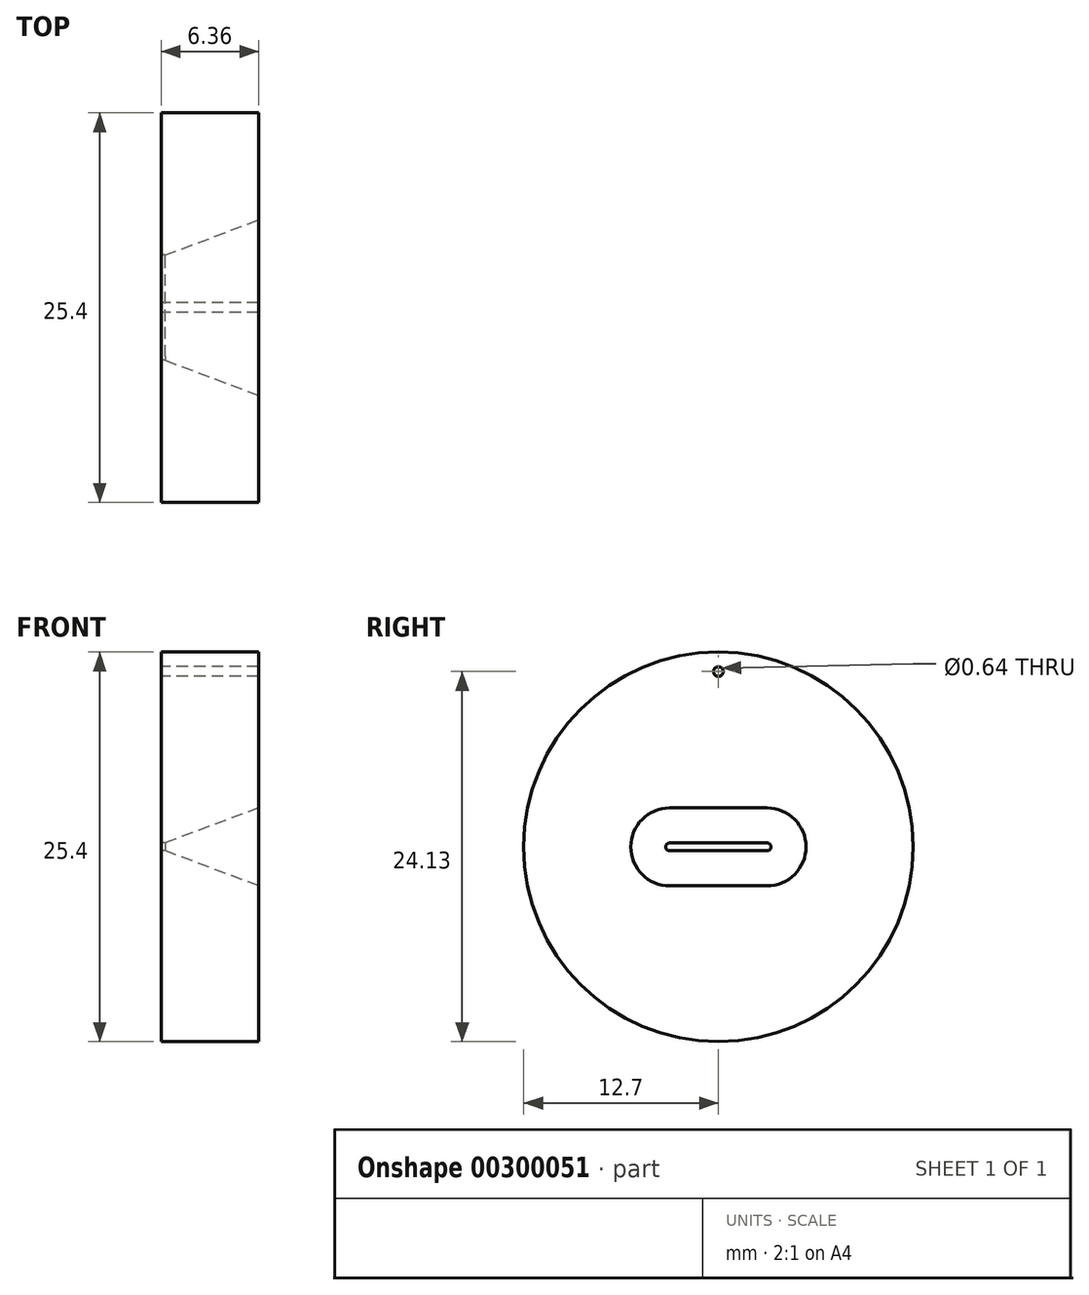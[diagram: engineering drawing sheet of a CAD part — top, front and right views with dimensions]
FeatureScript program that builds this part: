
annotation { "Feature Type Name" : "Feature", "Feature Type Description" : "" }
export const myFeature = defineFeature(function(context is Context, id is Id, definition is map)
    precondition{}
    {
        {
            var Q0;
            Q0=qCreatedBy(makeId("Right.planeOp"),FACE);
            var sketch = newSketch(context, id + "F0", { "sketchPlane" : qUnion([Q0])});
            skCircle(sketch, "E0", {"center": v(0, 0) * mm, "radius": 12.7 * mm});
            skSolve(sketch);
        }
        {
            var Q0;
            Q0 = qSketchRegion(id + "F0", true);
            extrude(context, id + "F1", {"entities" : qUnion([Q0]), "endBound" : BoundingType.SYMMETRIC, "depth" : 6.35 * mm});
        }
        {
            var Q0;
            Q0=makeQuery(id+"F1.opExtrude","CAP_FACE",FACE,{"disambiguationData":[OSD([sQuery(id+"F0.wireOp",EDGE,"E0")])],"isStart":true});
            var sketch = newSketch(context, id + "F2", { "sketchPlane" : qUnion([Q0])});
            skLineSegment(sketch, "E1", {"start": v(0, 13.8) * mm, "end": v(0, -8.5) * mm, "construction": true});
            skCircle(sketch, "E2", {"center": v(0, 11.43) * mm, "radius": 0.32 * mm});
            skSolve(sketch);
        }
        {
            var Q0;
            Q0=qCreatedBy(makeId("Front.planeOp"),FACE);
            var sketch = newSketch(context, id + "F3", { "sketchPlane" : qUnion([Q0])});
            skLineSegment(sketch, "E3", {"start": v(-29.97, 0) * mm, "end": v(27.38, 0) * mm, "construction": true});
            skSolve(sketch);
        }
        {
            var Q0;
            Q0 = qSketchRegion(id + "F2", true);
            extrude(context, id + "F4", {"entities" : qUnion([Q0]), "operationType" : NewBodyOperationType.REMOVE, "endBound" : BoundingType.THROUGH_ALL, "oppositeDirection" : true, "depth" : 25.4 * mm});
        }
        {
            var Q0;
            Q0=makeQuery(id+"F1.opExtrude","CAP_FACE",FACE,{"disambiguationData":[OSD([sQuery(id+"F0.wireOp",EDGE,"E0")])],"isStart":true});
            var sketch = newSketch(context, id + "F5", { "sketchPlane" : qUnion([Q0])});
            skLineSegment(sketch, "E4", {"start": v(0, 4.89) * mm, "end": v(0, -3.87) * mm, "construction": true});
            skArc(sketch, "E5", {"start": v(-3.17, -0.25) * mm, "mid": v(-3.43, 0) * mm, "end": v(-3.17, 0.25) * mm});
            skLineSegment(sketch, "E6", {"start": v(0, 0.25) * mm, "end": v(-3.17, 0.25) * mm});
            skLineSegment(sketch, "E7", {"start": v(0, -0.25) * mm, "end": v(-3.17, -0.25) * mm});
            skLineSegment(sketch, "E8.MirrorCS", {"start": v(0, 0.25) * mm, "end": v(3.18, 0.25) * mm});
            skLineSegment(sketch, "E9.MirrorCS", {"start": v(0, -0.25) * mm, "end": v(3.18, -0.25) * mm});
            skArc(sketch, "E10.MirrorCS", {"start": v(3.18, -0.25) * mm, "mid": v(3.43, 0) * mm, "end": v(3.18, 0.25) * mm});
            skSolve(sketch);
        }
        {
            var Q0;
            Q0=makeQuery(id+"F1.opExtrude","CAP_FACE",FACE,{"disambiguationData":[OSD([sQuery(id+"F0.wireOp",EDGE,"E0")])],"isStart":false});
            var sketch = newSketch(context, id + "F6", { "sketchPlane" : qUnion([Q0])});
            skLineSegment(sketch, "E11", {"start": v(0, 5.57) * mm, "end": v(0, -3.68) * mm, "construction": true});
            skArc(sketch, "E12", {"start": v(-3.18, -2.54) * mm, "mid": v(-5.72, 0) * mm, "end": v(-3.17, 2.54) * mm});
            skLineSegment(sketch, "E13", {"start": v(-3.17, 2.54) * mm, "end": v(0, 2.54) * mm});
            skLineSegment(sketch, "E14", {"start": v(0, -2.54) * mm, "end": v(-3.17, -2.54) * mm});
            skLineSegment(sketch, "E15.MirrorCS", {"start": v(3.17, 2.54) * mm, "end": v(0, 2.54) * mm});
            skLineSegment(sketch, "E16.MirrorCS", {"start": v(0, -2.54) * mm, "end": v(3.18, -2.54) * mm});
            skArc(sketch, "E17.MirrorCS", {"start": v(3.18, -2.54) * mm, "mid": v(5.72, 0) * mm, "end": v(3.17, 2.54) * mm});
            skSolve(sketch);
        }
        {
            var Q0;
            Q0 = qSketchRegion(id + "F5", true);
            extrude(context, id + "F7", {"entities" : qUnion([Q0]), "operationType" : NewBodyOperationType.REMOVE, "oppositeDirection" : true, "depth" : 0.25 * mm, "offsetDistance" : 25.4 * mm});
        }
        {
            var Q0;
            Q0=makeQuery(id+"F7.boolean.opBoolean","COPY",FACE,{"derivedFrom":makeQuery(id+"F7.opExtrude","CAP_FACE",FACE,{"disambiguationData":[OSD([sQuery(id+"F5.wireOp",EDGE,"E5"),sQuery(id+"F5.wireOp",EDGE,"E6"),sQuery(id+"F5.wireOp",EDGE,"E7"),sQuery(id+"F5.wireOp",EDGE,"E8.MirrorCS"),sQuery(id+"F5.wireOp",EDGE,"E9.MirrorCS"),sQuery(id+"F5.wireOp",EDGE,"E10.MirrorCS")])],"isStart":false})});
            var sketch = newSketch(context, id + "F8", { "sketchPlane" : qUnion([Q0])});
            skLineSegment(sketch, "E18", {"start": v(0, 2.37) * mm, "end": v(0, -2.05) * mm, "construction": true});
            skArc(sketch, "E19", {"start": v(-3.17, -0.25) * mm, "mid": v(-3.43, 0) * mm, "end": v(-3.18, 0.25) * mm});
            skLineSegment(sketch, "E20", {"start": v(-3.18, 0.25) * mm, "end": v(0, 0.25) * mm});
            skLineSegment(sketch, "E21", {"start": v(-3.17, -0.25) * mm, "end": v(0, -0.25) * mm});
            skLineSegment(sketch, "E22.MirrorCS", {"start": v(3.18, 0.25) * mm, "end": v(0, 0.25) * mm});
            skLineSegment(sketch, "E23.MirrorCS", {"start": v(3.18, -0.25) * mm, "end": v(0, -0.25) * mm});
            skArc(sketch, "E24.MirrorCS", {"start": v(3.18, -0.25) * mm, "mid": v(3.43, 0) * mm, "end": v(3.18, 0.25) * mm});
            skSolve(sketch);
        }
        {
            var Q1;
            Q1 = qSketchRegion(id + "F6", true);
            var Q2;
            Q2 = qSketchRegion(id + "F8", true);
            loft(context, id + "F9", {"operationType" : NewBodyOperationType.REMOVE, "sheetProfilesArray" : [{ "sheetProfileEntities" : qUnion([Q1]) }, { "sheetProfileEntities" : qUnion([Q2]) }]});
        }
    });
